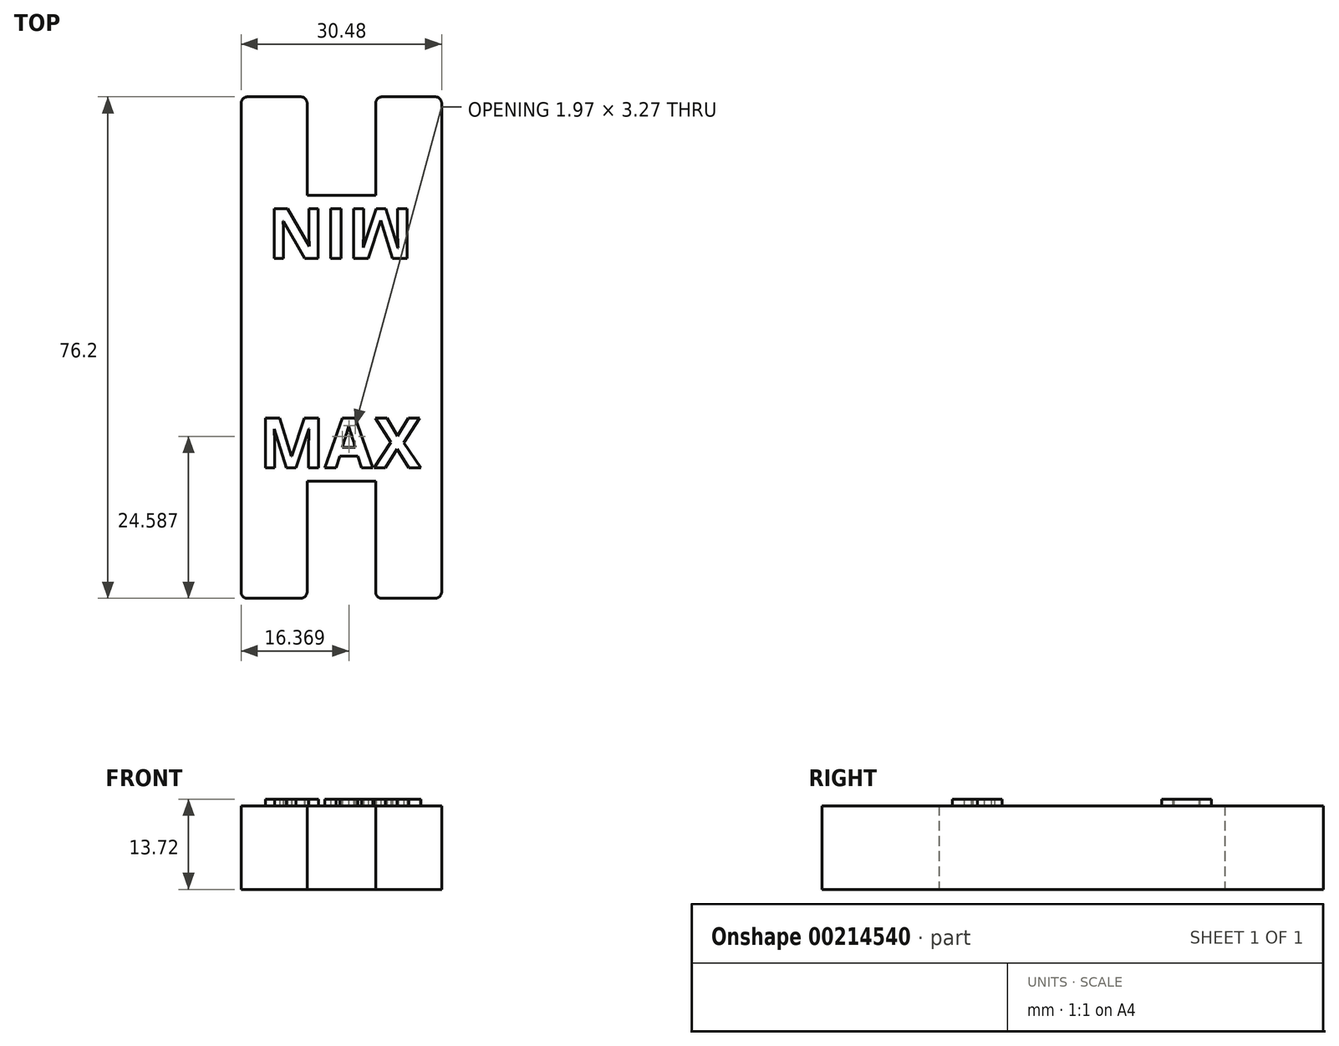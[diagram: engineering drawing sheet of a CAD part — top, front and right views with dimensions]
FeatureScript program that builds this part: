
annotation { "Feature Type Name" : "Feature", "Feature Type Description" : "" }
export const myFeature = defineFeature(function(context is Context, id is Id, definition is map)
    precondition{}
    {
        {
            var Q0;
            Q0=qCreatedBy(makeId("Top.planeOp"),FACE);
            var sketch = newSketch(context, id + "F0", { "sketchPlane" : qUnion([Q0])});
            skLineSegment(sketch, "E0.bottom", {"start": v(-15.24, 38.1) * mm, "end": v(-5.2, 38.1) * mm});
            skLineSegment(sketch, "E0.top", {"start": v(-15.24, -38.1) * mm, "end": v(-5.2, -38.1) * mm});
            skLineSegment(sketch, "E0.left", {"start": v(-15.24, 38.1) * mm, "end": v(-15.24, -38.1) * mm});
            skLineSegment(sketch, "E0.right", {"start": v(15.24, 38.1) * mm, "end": v(15.24, -38.1) * mm});
            skPoint(sketch, "E0.middle", {"position": v(0, 0) * mm});
            skLineSegment(sketch, "E1.bottom", {"start": v(-5.2, -20.32) * mm, "end": v(5.2, -20.32) * mm});
            skLineSegment(sketch, "E1.left", {"start": v(-5.2, -20.32) * mm, "end": v(-5.2, -38.1) * mm});
            skLineSegment(sketch, "E1.right", {"start": v(5.2, -20.32) * mm, "end": v(5.2, -38.1) * mm});
            skPoint(sketch, "E1.middle", {"position": v(0, -29.21) * mm});
            skLineSegment(sketch, "E2.trimOffspring", {"start": v(5.2, -38.1) * mm, "end": v(15.24, -38.1) * mm});
            skLineSegment(sketch, "E3.bottom", {"start": v(5.2, 23.11) * mm, "end": v(-5.2, 23.11) * mm});
            skLineSegment(sketch, "E3.left", {"start": v(5.2, 23.11) * mm, "end": v(5.2, 38.1) * mm});
            skLineSegment(sketch, "E3.right", {"start": v(-5.2, 23.11) * mm, "end": v(-5.2, 38.1) * mm});
            skPoint(sketch, "E3.middle", {"position": v(0, 30.6) * mm});
            skLineSegment(sketch, "E4.trimOffspring", {"start": v(5.2, 38.1) * mm, "end": v(15.24, 38.1) * mm});
            skSolve(sketch);
        }
        {
            var Q0;
            Q0 = qSketchRegion(id + "F0", true);
            extrude(context, id + "F1", {"entities" : qUnion([Q0]), "depth" : 12.7 * mm});
        }
        {
            var Q0;
            Q0=makeQuery(id+"F1.opExtrude","CAP_FACE",FACE,{"disambiguationData":[OSD([sQuery(id+"F0.wireOp",EDGE,"E0.bottom"),sQuery(id+"F0.wireOp",EDGE,"E0.top"),sQuery(id+"F0.wireOp",EDGE,"E0.left"),sQuery(id+"F0.wireOp",EDGE,"E0.right"),sQuery(id+"F0.wireOp",EDGE,"E1.bottom"),sQuery(id+"F0.wireOp",EDGE,"E1.left"),sQuery(id+"F0.wireOp",EDGE,"E1.right"),sQuery(id+"F0.wireOp",EDGE,"E2.trimOffspring"),sQuery(id+"F0.wireOp",EDGE,"E3.bottom"),sQuery(id+"F0.wireOp",EDGE,"E3.left"),sQuery(id+"F0.wireOp",EDGE,"E3.right"),sQuery(id+"F0.wireOp",EDGE,"E4.trimOffspring")])],"isStart":false});
            var sketch = newSketch(context, id + "F2", { "sketchPlane" : qUnion([Q0])});
            skText(sketch, "E5", { "text": "MAX", "fontName": "OpenSans-Bold.ttf"});
            skText(sketch, "E6", { "text": "MIN", "fontName": "OpenSans-Bold.ttf"});
            const initialGuessF2  = {"E5": [-0.01251, -0.01829, 1, 0, 0.00762], "E6": [0.01091, 0.02108, -1, 0, 0.00762]};
            skSetInitialGuess(sketch, initialGuessF2);
            skSolve(sketch);
        }
        {
            var Q0;
            Q0 = qSketchRegion(id + "F2", true);
            extrude(context, id + "F3", {"entities" : qUnion([Q0]), "depth" : 1.02 * mm});
        }
        {
            var Q0;
            Q0=makeQuery(id+"F1.opExtrude","SWEPT_EDGE",EDGE,{"disambiguationData":[OSD([sQuery(id+"F0.wireOp",EDGE,"E3.left"),sQuery(id+"F0.wireOp",EDGE,"E4.trimOffspring")])]});
            var Q1;
            Q1=makeQuery(id+"F1.opExtrude","SWEPT_EDGE",EDGE,{"disambiguationData":[OSD([sQuery(id+"F0.wireOp",EDGE,"E0.bottom"),sQuery(id+"F0.wireOp",EDGE,"E3.right")])]});
            var Q2;
            Q2=makeQuery(id+"F1.opExtrude","SWEPT_EDGE",EDGE,{"disambiguationData":[OSD([sQuery(id+"F0.wireOp",EDGE,"E0.bottom"),sQuery(id+"F0.wireOp",EDGE,"E0.left")])]});
            var Q3;
            Q3=makeQuery(id+"F1.opExtrude","SWEPT_EDGE",EDGE,{"disambiguationData":[OSD([sQuery(id+"F0.wireOp",EDGE,"E0.right"),sQuery(id+"F0.wireOp",EDGE,"E4.trimOffspring")])]});
            var Q4;
            Q4=makeQuery(id+"F1.opExtrude","SWEPT_EDGE",EDGE,{"disambiguationData":[OSD([sQuery(id+"F0.wireOp",EDGE,"E0.top"),sQuery(id+"F0.wireOp",EDGE,"E0.left")])]});
            var Q5;
            Q5=makeQuery(id+"F1.opExtrude","SWEPT_EDGE",EDGE,{"disambiguationData":[OSD([sQuery(id+"F0.wireOp",EDGE,"E0.top"),sQuery(id+"F0.wireOp",EDGE,"E1.left")])]});
            var Q6;
            Q6=makeQuery(id+"F1.opExtrude","SWEPT_EDGE",EDGE,{"disambiguationData":[OSD([sQuery(id+"F0.wireOp",EDGE,"E1.right"),sQuery(id+"F0.wireOp",EDGE,"E2.trimOffspring")])]});
            var Q7;
            Q7=makeQuery(id+"F1.opExtrude","SWEPT_EDGE",EDGE,{"disambiguationData":[OSD([sQuery(id+"F0.wireOp",EDGE,"E0.right"),sQuery(id+"F0.wireOp",EDGE,"E2.trimOffspring")])]});
            fillet(context, id + "F4", {"entities" : qUnion([Q0, Q1, Q2, Q3, Q4, Q5, Q6, Q7]), "radius" : 1 * mm, "tangentPropagation" : true, "allowEdgeOverflow" : false});
        }
    });
